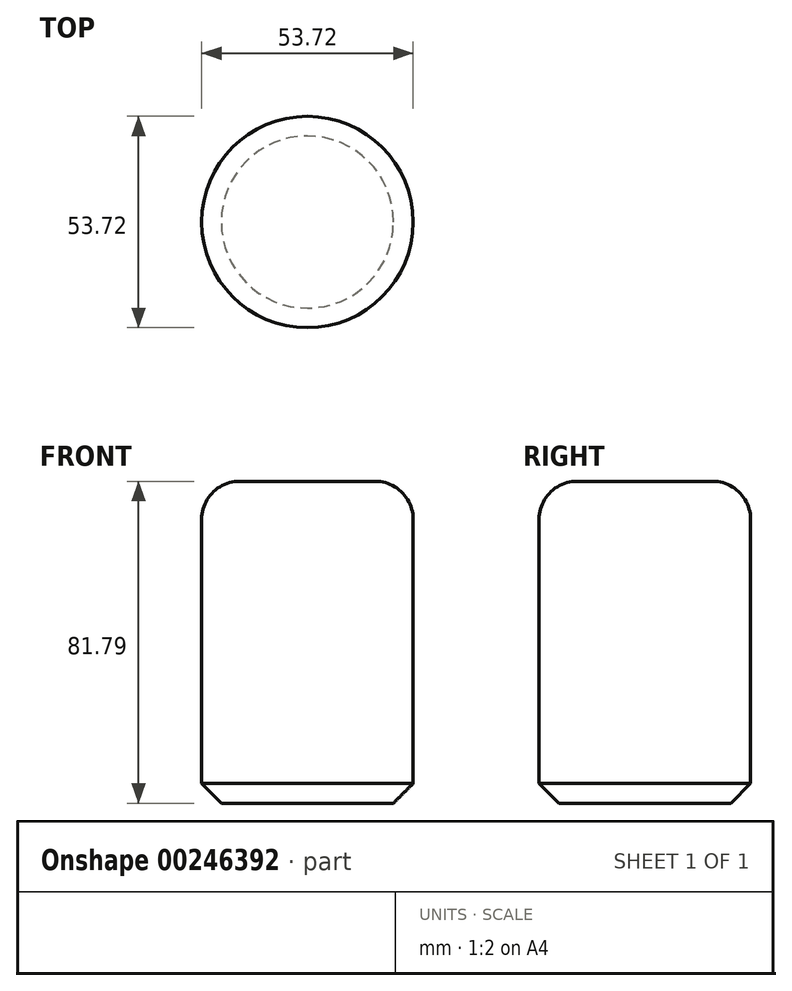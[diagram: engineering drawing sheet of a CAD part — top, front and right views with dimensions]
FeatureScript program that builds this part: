
annotation { "Feature Type Name" : "Feature", "Feature Type Description" : "" }
export const myFeature = defineFeature(function(context is Context, id is Id, definition is map)
    precondition{}
    {
        {
            var Q0;
            Q0=qCreatedBy(makeId("Top.planeOp"),FACE);
            var sketch = newSketch(context, id + "F0", { "sketchPlane" : qUnion([Q0])});
            skCircle(sketch, "E0", {"center": v(-7.9, 8.01) * mm, "radius": 26.86 * mm});
            skSolve(sketch);
        }
        {
            var Q0;
            Q0 = qSketchRegion(id + "F0", true);
            extrude(context, id + "F1", {"entities" : qUnion([Q0]), "depth" : 81.8 * mm});
        }
        {
            var Q0;
            Q0=makeQuery(id+"F1.opExtrude","CAP_EDGE",EDGE,{"disambiguationData":[OSD([sQuery(id+"F0.wireOp",EDGE,"E0")])],"isStart":false});
            fillet(context, id + "F2", {"entities" : qUnion([Q0]), "radius" : 9.66 * mm, "tangentPropagation" : true, "allowEdgeOverflow" : false});
        }
        {
            var Q0;
            Q0=makeQuery(id+"F1.opExtrude","CAP_EDGE",EDGE,{"disambiguationData":[OSD([sQuery(id+"F0.wireOp",EDGE,"E0")])],"isStart":true});
            chamfer(context, id + "F3", {"entities" : qUnion([Q0]), "width" : 5 * mm, "tangentPropagation" : true});
        }
    });
